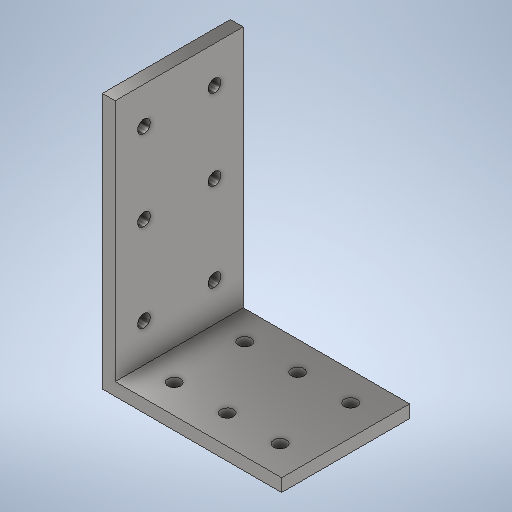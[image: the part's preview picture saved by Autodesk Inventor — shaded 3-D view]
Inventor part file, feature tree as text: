
AUTODESK INVENTOR PART (.ipt)
format: ipt  version: 2025.2 (Build 292293000, 293)  size: 278,016 bytes
history: native  units: in
note: dims shown in document units (in); Inventor stores cm internally (conversion verified against a paired STEP export)
features: extrude x3, sketch x2
ambient origin geometry x8: Origin, YZ Plane, XZ Plane, XY Plane, X Axis, Y Axis, Z Axis, Center Point
bodies: Solid1 (feature_tree)
feature tree (5):
  extrude  "Extrusion1"  Depth=5.0in
  extrude  "Extrusion2"  Depth=2.5in TaperAngle=0.0deg
  extrude  "Extrusion3"  Depth=0.25in
  sketch  "Sketch1"  dims[d0=3.5in d1=5.0in]
  sketch  "Sketch3"  dims[d2=0.25in d3=2.5in d4=0.0in d5=0.25in d6=0.25in d7=2.5in d9=3.5in d10=0.5906in d12=0.0in d13=0.0in d14=1.378in d15=1.5748in d16=1.5in d17=0.25in d18=0.0in d19=0.0in d20=4.0in d21=1.378in]
